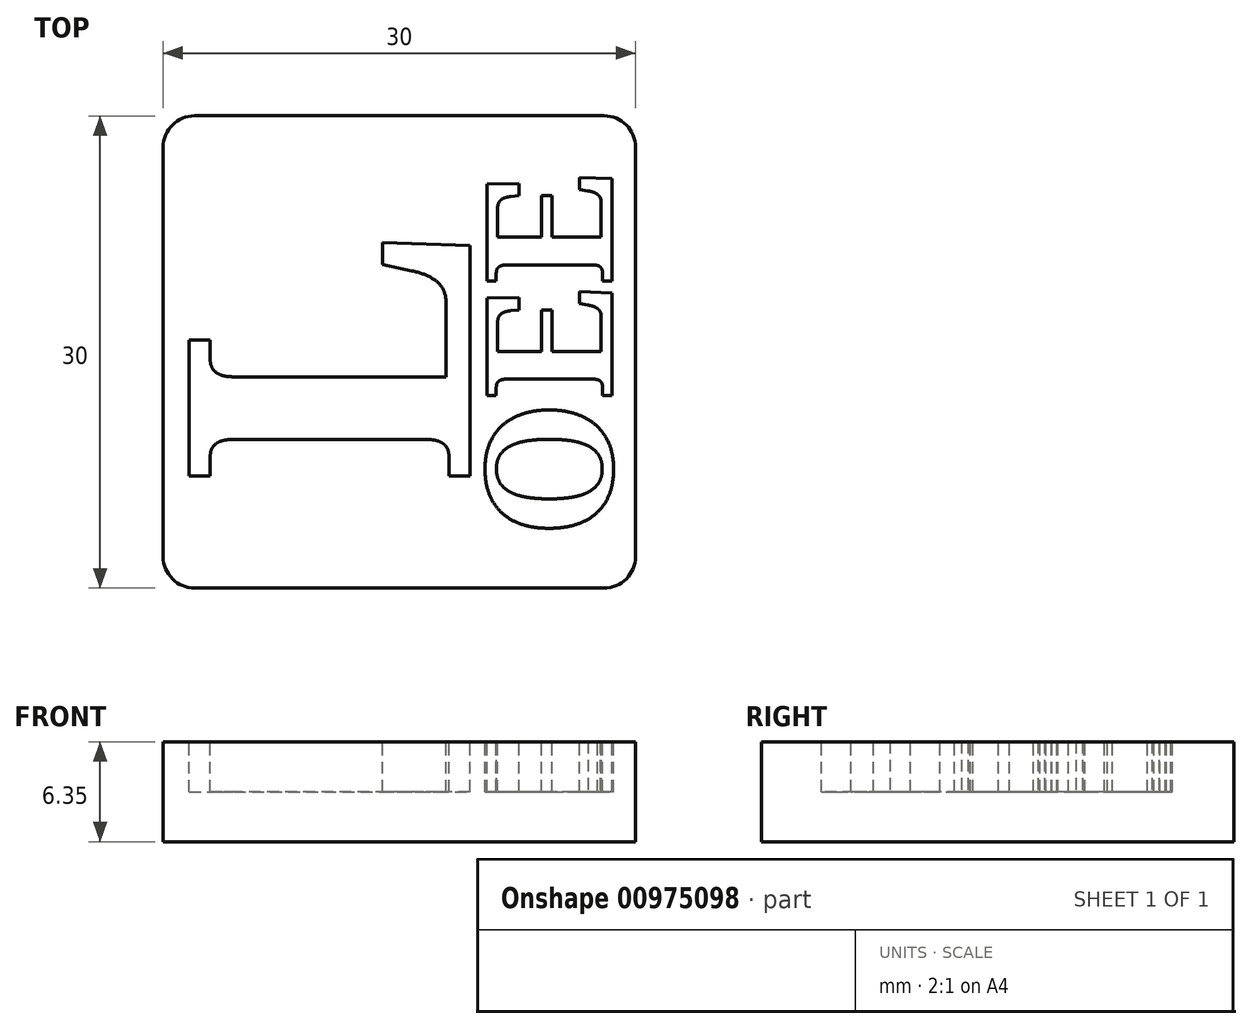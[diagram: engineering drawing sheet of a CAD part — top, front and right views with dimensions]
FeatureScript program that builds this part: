
annotation { "Feature Type Name" : "Feature", "Feature Type Description" : "" }
export const myFeature = defineFeature(function(context is Context, id is Id, definition is map)
    precondition{}
    {
        {
            var Q0;
            Q0=qCreatedBy(makeId("Top.planeOp"),FACE);
            var sketch = newSketch(context, id + "F0", { "sketchPlane" : qUnion([Q0])});
            skLineSegment(sketch, "E0.bottom", {"start": v(-15.27, 9.73) * mm, "end": v(10.73, 9.73) * mm});
            skLineSegment(sketch, "E0.top", {"start": v(-15.27, -20.27) * mm, "end": v(10.73, -20.27) * mm});
            skLineSegment(sketch, "E0.left", {"start": v(-17.27, 7.73) * mm, "end": v(-17.27, -18.27) * mm});
            skLineSegment(sketch, "E0.right", {"start": v(12.73, 7.73) * mm, "end": v(12.73, -18.27) * mm});
            skPoint(sketch, "E1.visualSharp", {"position": v(-17.27, 9.73) * mm});
            skArc(sketch, "E1.filletArc", {"start": v(-15.27, 9.73) * mm, "mid": v(-16.68, 9.15) * mm, "end": v(-17.27, 7.73) * mm});
            skPoint(sketch, "E2.visualSharp", {"position": v(12.73, 9.73) * mm});
            skArc(sketch, "E2.filletArc", {"start": v(12.73, 7.73) * mm, "mid": v(12.14, 9.15) * mm, "end": v(10.73, 9.73) * mm});
            skPoint(sketch, "E3.visualSharp", {"position": v(12.73, -20.27) * mm});
            skArc(sketch, "E3.filletArc", {"start": v(10.73, -20.27) * mm, "mid": v(12.14, -19.68) * mm, "end": v(12.73, -18.27) * mm});
            skPoint(sketch, "E4.visualSharp", {"position": v(-17.27, -20.27) * mm});
            skArc(sketch, "E4.filletArc", {"start": v(-17.27, -18.27) * mm, "mid": v(-16.68, -19.68) * mm, "end": v(-15.27, -20.27) * mm});
            skSolve(sketch);
        }
        {
            var Q0;
            Q0=qSketchRegion(id+"F0",true);
            extrude(context, id + "F1", {"entities" : qUnion([Q0]), "depth" : 6.35 * mm, "offsetDistance" : 25.4 * mm});
        }
        {
            var Q0;
            Q0=makeQuery(id+"F1.opExtrude","CAP_FACE",FACE,{"disambiguationData":[OSD([sQuery(id+"F0.wireOp",EDGE,"E0.bottom"),sQuery(id+"F0.wireOp",EDGE,"E0.top"),sQuery(id+"F0.wireOp",EDGE,"E0.left"),sQuery(id+"F0.wireOp",EDGE,"E0.right")])],"isStart":false});
            var sketch = newSketch(context, id + "F2", { "sketchPlane" : qUnion([Q0])});
            skText(sketch, "E5", { "text": "L", "fontName": "NotoSerif-Bold.ttf"});
            skText(sketch, "E6", { "text": "OEE", "fontName": "NotoSerif-Bold.ttf"});
            skPoint(sketch, "E7", {"position": v(-17.27, -5.27) * mm});
            skPoint(sketch, "E8", {"position": v(12.73, -5.27) * mm});
            const initialGuessF2  = {"E5": [0.00223, -0.01384, 0, 1, 0.018], "E6": [0.01123, -0.01708, 0, 1, 0.008]};
            skSetInitialGuess(sketch, initialGuessF2);
            skSolve(sketch);
        }
        {
            var Q0;
            Q0=qSketchRegion(id+"F2",true);
            extrude(context, id + "F3", {"entities" : qUnion([Q0]), "operationType" : NewBodyOperationType.REMOVE, "oppositeDirection" : true, "depth" : 3.17 * mm, "offsetDistance" : 25.4 * mm});
        }
    });
